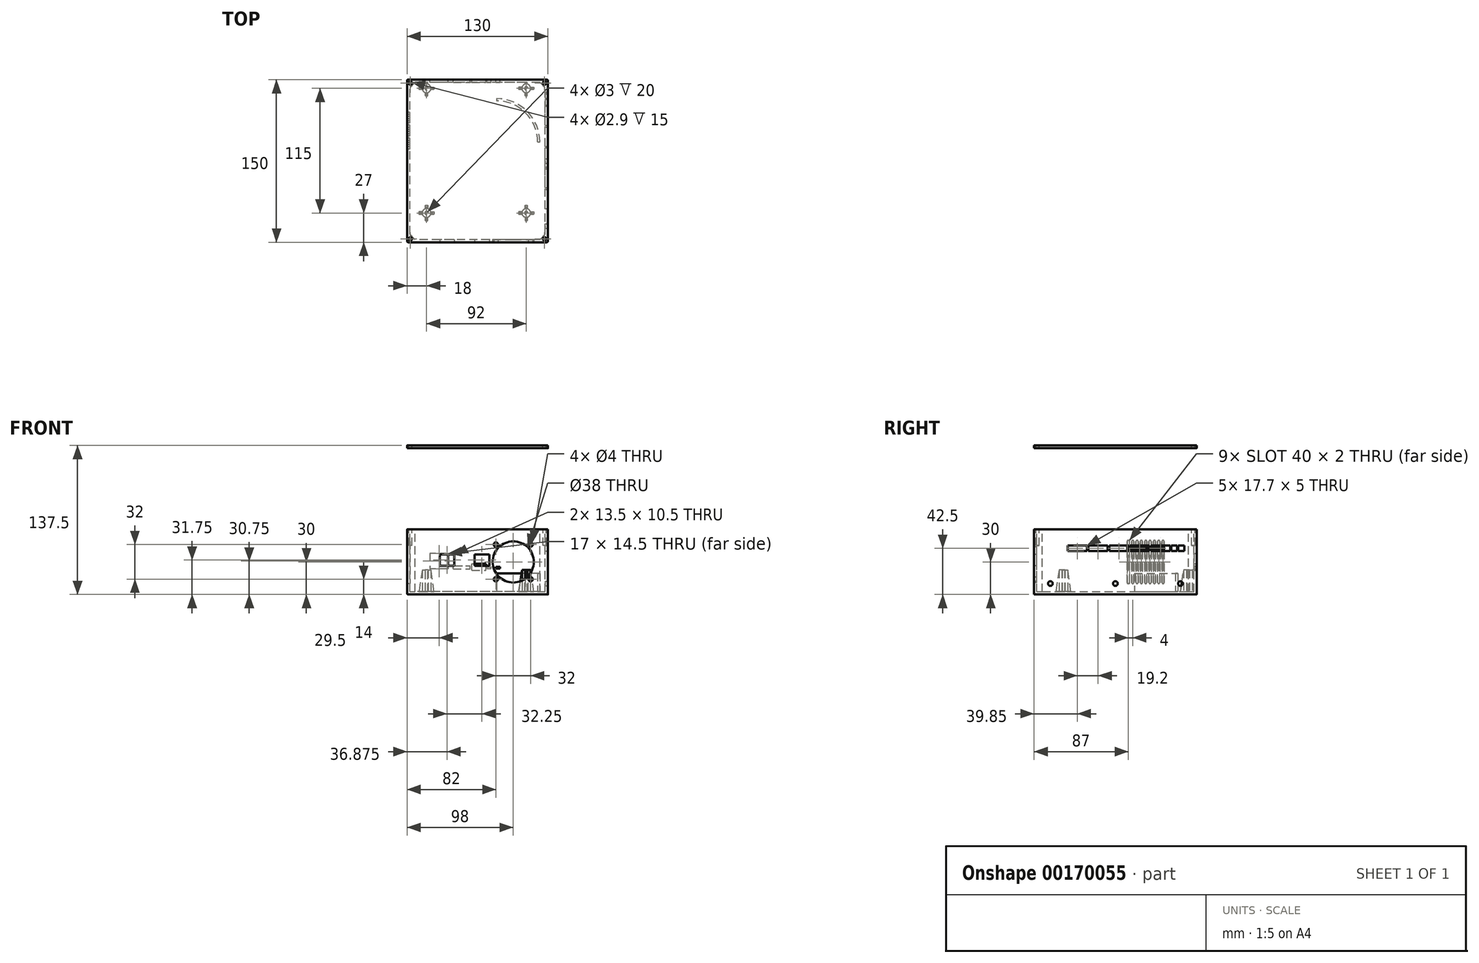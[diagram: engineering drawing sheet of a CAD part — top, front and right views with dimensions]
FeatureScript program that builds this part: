
annotation { "Feature Type Name" : "Feature", "Feature Type Description" : "" }
export const myFeature = defineFeature(function(context is Context, id is Id, definition is map)
    precondition{}
    {
        {
            var Q0;
            Q0=qCreatedBy(makeId("Top.planeOp"),FACE);
            var sketch = newSketch(context, id + "F0", { "sketchPlane" : qUnion([Q0])});
            skLineSegment(sketch, "E0.bottom", {"start": v(65, -75) * mm, "end": v(-65, -75) * mm});
            skLineSegment(sketch, "E0.top", {"start": v(65, 75) * mm, "end": v(-65, 75) * mm});
            skLineSegment(sketch, "E0.left", {"start": v(65, -75) * mm, "end": v(65, 75) * mm});
            skLineSegment(sketch, "E0.right", {"start": v(-65, -75) * mm, "end": v(-65, 75) * mm});
            skPoint(sketch, "E0.middle", {"position": v(0, 0) * mm});
            skCircle(sketch, "E1", {"center": v(-47, 67) * mm, "radius": 1.5 * mm});
            skCircle(sketch, "E2", {"center": v(45, 67) * mm, "radius": 1.5 * mm});
            skCircle(sketch, "E3", {"center": v(45, -48) * mm, "radius": 1.5 * mm});
            skCircle(sketch, "E4", {"center": v(-47, -48) * mm, "radius": 1.5 * mm});
            skCircle(sketch, "E5", {"center": v(-47, -48) * mm, "radius": 4 * mm});
            skCircle(sketch, "E6", {"center": v(45, -48) * mm, "radius": 4 * mm});
            skCircle(sketch, "E7", {"center": v(45, 67) * mm, "radius": 4 * mm});
            skCircle(sketch, "E8", {"center": v(-47, 67) * mm, "radius": 4 * mm});
            skLineSegment(sketch, "E9.bottom", {"start": v(46, 74) * mm, "end": v(44, 74) * mm});
            skLineSegment(sketch, "E9.top", {"start": v(46, 60) * mm, "end": v(44, 60) * mm});
            skLineSegment(sketch, "E9.left", {"start": v(46, 74) * mm, "end": v(46, 70.87) * mm});
            skLineSegment(sketch, "E9.right", {"start": v(44, 74) * mm, "end": v(44, 70.87) * mm});
            skLineSegment(sketch, "E10.bottom", {"start": v(52, 66) * mm, "end": v(48.87, 66) * mm});
            skLineSegment(sketch, "E10.top", {"start": v(52, 68) * mm, "end": v(48.87, 68) * mm});
            skLineSegment(sketch, "E10.left", {"start": v(52, 66) * mm, "end": v(52, 68) * mm});
            skLineSegment(sketch, "E10.right", {"start": v(38, 66) * mm, "end": v(38, 68) * mm});
            skLineSegment(sketch, "E11.trimOffspring", {"start": v(41.13, 68) * mm, "end": v(38, 68) * mm});
            skLineSegment(sketch, "E12.trimOffspring", {"start": v(41.13, 66) * mm, "end": v(38, 66) * mm});
            skLineSegment(sketch, "E13.trimOffspring", {"start": v(44, 63.13) * mm, "end": v(44, 60) * mm});
            skLineSegment(sketch, "E14.trimOffspring", {"start": v(46, 63.13) * mm, "end": v(46, 60) * mm});
            skLineSegment(sketch, "E15.bottom", {"start": v(-40, 66) * mm, "end": v(-43.13, 66) * mm});
            skLineSegment(sketch, "E15.top", {"start": v(-40, 68) * mm, "end": v(-43.13, 68) * mm});
            skLineSegment(sketch, "E15.left", {"start": v(-40, 66) * mm, "end": v(-40, 68) * mm});
            skLineSegment(sketch, "E15.right", {"start": v(-54, 66) * mm, "end": v(-54, 68) * mm});
            skLineSegment(sketch, "E16.bottom", {"start": v(-46, 74) * mm, "end": v(-48, 74) * mm});
            skLineSegment(sketch, "E16.top", {"start": v(-46, 60) * mm, "end": v(-48, 60) * mm});
            skLineSegment(sketch, "E16.left", {"start": v(-46, 74) * mm, "end": v(-46, 70.87) * mm});
            skLineSegment(sketch, "E16.right", {"start": v(-48, 74) * mm, "end": v(-48, 70.87) * mm});
            skLineSegment(sketch, "E17.trimOffspring", {"start": v(-50.87, 68) * mm, "end": v(-54, 68) * mm});
            skLineSegment(sketch, "E18.trimOffspring", {"start": v(-50.87, 66) * mm, "end": v(-54, 66) * mm});
            skLineSegment(sketch, "E19.trimOffspring", {"start": v(-48, 63.13) * mm, "end": v(-48, 60) * mm});
            skLineSegment(sketch, "E20.trimOffspring", {"start": v(-46, 63.13) * mm, "end": v(-46, 60) * mm});
            skLineSegment(sketch, "E21.bottom", {"start": v(-40, -49) * mm, "end": v(-43.13, -49) * mm});
            skLineSegment(sketch, "E21.top", {"start": v(-40, -47) * mm, "end": v(-43.13, -47) * mm});
            skLineSegment(sketch, "E21.left", {"start": v(-40, -49) * mm, "end": v(-40, -47) * mm});
            skLineSegment(sketch, "E21.right", {"start": v(-54, -49) * mm, "end": v(-54, -47) * mm});
            skLineSegment(sketch, "E22.bottom", {"start": v(-46, -41) * mm, "end": v(-48, -41) * mm});
            skLineSegment(sketch, "E22.top", {"start": v(-46, -55) * mm, "end": v(-48, -55) * mm});
            skLineSegment(sketch, "E22.left", {"start": v(-46, -41) * mm, "end": v(-46, -44.13) * mm});
            skLineSegment(sketch, "E22.right", {"start": v(-48, -41) * mm, "end": v(-48, -44.13) * mm});
            skLineSegment(sketch, "E23.trimOffspring", {"start": v(-50.87, -49) * mm, "end": v(-54, -49) * mm});
            skLineSegment(sketch, "E24.trimOffspring", {"start": v(-50.87, -47) * mm, "end": v(-54, -47) * mm});
            skLineSegment(sketch, "E25.trimOffspring", {"start": v(-46, -51.87) * mm, "end": v(-46, -55) * mm});
            skLineSegment(sketch, "E26.trimOffspring", {"start": v(-48, -51.87) * mm, "end": v(-48, -55) * mm});
            skLineSegment(sketch, "E27.bottom", {"start": v(52, -49) * mm, "end": v(48.87, -49) * mm});
            skLineSegment(sketch, "E27.top", {"start": v(52, -47) * mm, "end": v(48.87, -47) * mm});
            skLineSegment(sketch, "E27.left", {"start": v(52, -49) * mm, "end": v(52, -47) * mm});
            skLineSegment(sketch, "E27.right", {"start": v(38, -49) * mm, "end": v(38, -47) * mm});
            skLineSegment(sketch, "E28.bottom", {"start": v(46, -55) * mm, "end": v(44, -55) * mm});
            skLineSegment(sketch, "E28.top", {"start": v(46, -41) * mm, "end": v(44, -41) * mm});
            skLineSegment(sketch, "E28.left", {"start": v(46, -55) * mm, "end": v(46, -51.87) * mm});
            skLineSegment(sketch, "E28.right", {"start": v(44, -55) * mm, "end": v(44, -51.87) * mm});
            skLineSegment(sketch, "E29.trimOffspring", {"start": v(41.13, -49) * mm, "end": v(38, -49) * mm});
            skLineSegment(sketch, "E30.trimOffspring", {"start": v(41.13, -47) * mm, "end": v(38, -47) * mm});
            skLineSegment(sketch, "E31.trimOffspring", {"start": v(44, -44.13) * mm, "end": v(44, -41) * mm});
            skLineSegment(sketch, "E32.trimOffspring", {"start": v(46, -44.13) * mm, "end": v(46, -41) * mm});
            skLineSegment(sketch, "E33", {"start": v(65, 65) * mm, "end": v(55, 75) * mm});
            skLineSegment(sketch, "E34", {"start": v(65, -65) * mm, "end": v(55, -75) * mm});
            skLineSegment(sketch, "E35", {"start": v(-55, 75) * mm, "end": v(-65, 65) * mm});
            skLineSegment(sketch, "E36", {"start": v(-65, -65) * mm, "end": v(-55, -75) * mm});
            skSolve(sketch);
        }
        {
            var Q0;
            Q0=makeQuery(id+"F0.imprint","IMPRINT",FACE,{"disambiguationData":[TD([[makeQuery(id+"F0.imprint","IMPRINT",EDGE,{"derivedFrom":sQuery(id+"F0.wireOp",EDGE,"E0.bottom")}),-1.0]])]});
            var Q1;
            Q1=makeQuery(id+"F0.imprint","IMPRINT",FACE,{"disambiguationData":[TD([[makeQuery(id+"F0.imprint","IMPRINT",EDGE,{"derivedFrom":sQuery(id+"F0.wireOp",EDGE,"E2")}),-1.0]])]});
            var Q2;
            Q2=makeQuery(id+"F0.imprint","IMPRINT",FACE,{"disambiguationData":[TD([[makeQuery(id+"F0.imprint","IMPRINT",EDGE,{"derivedFrom":sQuery(id+"F0.wireOp",EDGE,"E4")}),-1.0]])]});
            var Q3;
            Q3=makeQuery(id+"F0.imprint","IMPRINT",FACE,{"disambiguationData":[TD([[makeQuery(id+"F0.imprint","IMPRINT",EDGE,{"derivedFrom":sQuery(id+"F0.wireOp",EDGE,"E16.top")}),-1.0]])]});
            var Q4;
            Q4=makeQuery(id+"F0.imprint","IMPRINT",FACE,{"disambiguationData":[TD([[makeQuery(id+"F0.imprint","IMPRINT",EDGE,{"derivedFrom":sQuery(id+"F0.wireOp",EDGE,"E21.right")}),-1.0]])]});
            var Q5;
            Q5=makeQuery(id+"F0.imprint","IMPRINT",FACE,{"disambiguationData":[TD([[makeQuery(id+"F0.imprint","IMPRINT",EDGE,{"derivedFrom":sQuery(id+"F0.wireOp",EDGE,"E22.top")}),-1.0]])]});
            var Q6;
            Q6=makeQuery(id+"F0.imprint","IMPRINT",FACE,{"disambiguationData":[TD([[makeQuery(id+"F0.imprint","IMPRINT",EDGE,{"derivedFrom":sQuery(id+"F0.wireOp",EDGE,"E1")}),-1.0]])]});
            var Q7;
            Q7=makeQuery(id+"F0.imprint","IMPRINT",FACE,{"disambiguationData":[TD([[makeQuery(id+"F0.imprint","IMPRINT",EDGE,{"derivedFrom":sQuery(id+"F0.wireOp",EDGE,"E3")}),-1.0]])]});
            var Q8;
            Q8=makeQuery(id+"F0.imprint","IMPRINT",FACE,{"disambiguationData":[TD([[makeQuery(id+"F0.imprint","IMPRINT",EDGE,{"derivedFrom":sQuery(id+"F0.wireOp",EDGE,"E15.right")}),-1.0]])]});
            var Q9;
            Q9=makeQuery(id+"F0.imprint","IMPRINT",FACE,{"disambiguationData":[TD([[makeQuery(id+"F0.imprint","IMPRINT",EDGE,{"derivedFrom":sQuery(id+"F0.wireOp",EDGE,"E28.bottom")}),-1.0]])]});
            var Q10;
            {var subQ0=sQuery(id+"F0.wireOp",EDGE,"E10.bottom");Q10=makeQuery(id+"F0.imprint","IMPRINT",FACE,{"disambiguationData":[TD([[makeQuery(id+"F0.imprint","IMPRINT",EDGE,{"derivedFrom":subQ0}),-1.0]])]});}
            var Q11;
            Q11=makeQuery(id+"F0.imprint","IMPRINT",FACE,{"disambiguationData":[TD([[makeQuery(id+"F0.imprint","IMPRINT",EDGE,{"derivedFrom":sQuery(id+"F0.wireOp",EDGE,"E9.top")}),-1.0]])]});
            var Q12;
            {var subQ0=sQuery(id+"F0.wireOp",EDGE,"E21.bottom");Q12=makeQuery(id+"F0.imprint","IMPRINT",FACE,{"disambiguationData":[TD([[makeQuery(id+"F0.imprint","IMPRINT",EDGE,{"derivedFrom":subQ0}),-1.0]])]});}
            var Q13;
            Q13=makeQuery(id+"F0.imprint","IMPRINT",FACE,{"disambiguationData":[TD([[makeQuery(id+"F0.imprint","IMPRINT",EDGE,{"derivedFrom":sQuery(id+"F0.wireOp",EDGE,"E28.top")}),1.0]])]});
            var Q14;
            Q14=makeQuery(id+"F0.imprint","IMPRINT",FACE,{"disambiguationData":[TD([[makeQuery(id+"F0.imprint","IMPRINT",EDGE,{"derivedFrom":sQuery(id+"F0.wireOp",EDGE,"E27.right")}),-1.0]])]});
            var Q15;
            Q15=makeQuery(id+"F0.imprint","IMPRINT",FACE,{"disambiguationData":[TD([[makeQuery(id+"F0.imprint","IMPRINT",EDGE,{"derivedFrom":sQuery(id+"F0.wireOp",EDGE,"E22.bottom")}),1.0]])]});
            var Q16;
            {var subQ0=sQuery(id+"F0.wireOp",EDGE,"E15.bottom");Q16=makeQuery(id+"F0.imprint","IMPRINT",FACE,{"disambiguationData":[TD([[makeQuery(id+"F0.imprint","IMPRINT",EDGE,{"derivedFrom":subQ0}),-1.0]])]});}
            var Q17;
            Q17=makeQuery(id+"F0.imprint","IMPRINT",FACE,{"disambiguationData":[TD([[makeQuery(id+"F0.imprint","IMPRINT",EDGE,{"derivedFrom":sQuery(id+"F0.wireOp",EDGE,"E9.bottom")}),1.0]])]});
            var Q18;
            {var subQ0=sQuery(id+"F0.wireOp",EDGE,"E27.bottom");Q18=makeQuery(id+"F0.imprint","IMPRINT",FACE,{"disambiguationData":[TD([[makeQuery(id+"F0.imprint","IMPRINT",EDGE,{"derivedFrom":subQ0}),-1.0]])]});}
            var Q19;
            Q19=makeQuery(id+"F0.imprint","IMPRINT",FACE,{"disambiguationData":[TD([[makeQuery(id+"F0.imprint","IMPRINT",EDGE,{"derivedFrom":sQuery(id+"F0.wireOp",EDGE,"E10.right")}),-1.0]])]});
            var Q20;
            Q20=makeQuery(id+"F0.imprint","IMPRINT",FACE,{"disambiguationData":[TD([[makeQuery(id+"F0.imprint","IMPRINT",EDGE,{"derivedFrom":sQuery(id+"F0.wireOp",EDGE,"E16.bottom")}),1.0]])]});
            var Q21;
            Q21=makeQuery(id+"F0.imprint","IMPRINT",FACE,{"disambiguationData":[TD([[makeQuery(id+"F0.imprint","IMPRINT",EDGE,{"derivedFrom":sQuery(id+"F0.wireOp",EDGE,"E2")}),1.0]])]});
            var Q22;
            Q22=makeQuery(id+"F0.imprint","IMPRINT",FACE,{"disambiguationData":[TD([[makeQuery(id+"F0.imprint","IMPRINT",EDGE,{"derivedFrom":sQuery(id+"F0.wireOp",EDGE,"E1")}),1.0]])]});
            var Q23;
            Q23=makeQuery(id+"F0.imprint","IMPRINT",FACE,{"disambiguationData":[TD([[makeQuery(id+"F0.imprint","IMPRINT",EDGE,{"derivedFrom":sQuery(id+"F0.wireOp",EDGE,"E4")}),1.0]])]});
            var Q24;
            Q24=makeQuery(id+"F0.imprint","IMPRINT",FACE,{"disambiguationData":[TD([[makeQuery(id+"F0.imprint","IMPRINT",EDGE,{"derivedFrom":sQuery(id+"F0.wireOp",EDGE,"E3")}),1.0]])]});
            var Q25;
            Q25=makeQuery(id+"F0.imprint","IMPRINT",FACE,{"disambiguationData":[TD([[makeQuery(id+"F0.imprint","IMPRINT",EDGE,{"derivedFrom":sQuery(id+"F0.wireOp",EDGE,"E9.bottom")}),-1.0]])]});
            var Q26;
            {var subQ3=sQuery(id+"F0.wireOp",EDGE,"E33");Q26=makeQuery(id+"F0.imprint","IMPRINT",FACE,{"disambiguationData":[TD([[makeQuery(id+"F0.imprint","IMPRINT",EDGE,{"derivedFrom":subQ3}),-1.0]])]});}
            var Q27;
            {var subQ3=sQuery(id+"F0.wireOp",EDGE,"E35");Q27=makeQuery(id+"F0.imprint","IMPRINT",FACE,{"disambiguationData":[TD([[makeQuery(id+"F0.imprint","IMPRINT",EDGE,{"derivedFrom":subQ3}),-1.0]])]});}
            extrude(context, id + "F1", {"entities" : qUnion([Q0, Q1, Q2, Q3, Q4, Q5, Q6, Q7, Q8, Q9, Q10, Q11, Q12, Q13, Q14, Q15, Q16, Q17, Q18, Q19, Q20, Q21, Q22, Q23, Q24, Q25, Q26, Q27]), "depth" : 60 * mm});
        }
        {
            var Q0;
            Q0=makeQuery(id+"F1.opExtrude","CAP_FACE",FACE,{"disambiguationData":[OSD([sQuery(id+"F0.wireOp",EDGE,"E0.bottom"),sQuery(id+"F0.wireOp",EDGE,"E0.top"),sQuery(id+"F0.wireOp",EDGE,"E0.left"),sQuery(id+"F0.wireOp",EDGE,"E0.right")])],"isStart":false});
            shell(context, id + "F2", {"entities" : qUnion([Q0]), "thickness" : 2.5 * mm});
        }
        {
            var Q0;
            Q0=makeQuery(id+"F0.imprint","IMPRINT",FACE,{"disambiguationData":[TD([[makeQuery(id+"F0.imprint","IMPRINT",EDGE,{"derivedFrom":sQuery(id+"F0.wireOp",EDGE,"E1")}),-1.0]])]});
            var Q1;
            Q1=makeQuery(id+"F0.imprint","IMPRINT",FACE,{"disambiguationData":[TD([[makeQuery(id+"F0.imprint","IMPRINT",EDGE,{"derivedFrom":sQuery(id+"F0.wireOp",EDGE,"E4")}),-1.0]])]});
            var Q2;
            Q2=makeQuery(id+"F0.imprint","IMPRINT",FACE,{"disambiguationData":[TD([[makeQuery(id+"F0.imprint","IMPRINT",EDGE,{"derivedFrom":sQuery(id+"F0.wireOp",EDGE,"E3")}),-1.0]])]});
            var Q3;
            Q3=makeQuery(id+"F0.imprint","IMPRINT",FACE,{"disambiguationData":[TD([[makeQuery(id+"F0.imprint","IMPRINT",EDGE,{"derivedFrom":sQuery(id+"F0.wireOp",EDGE,"E2")}),-1.0]])]});
            var Q4;
            {var subQ0=sQuery(id+"F0.wireOp",EDGE,"E10.bottom");Q4=makeQuery(id+"F0.imprint","IMPRINT",FACE,{"disambiguationData":[TD([[makeQuery(id+"F0.imprint","IMPRINT",EDGE,{"derivedFrom":subQ0}),-1.0]])]});}
            var Q5;
            Q5=makeQuery(id+"F0.imprint","IMPRINT",FACE,{"disambiguationData":[TD([[makeQuery(id+"F0.imprint","IMPRINT",EDGE,{"derivedFrom":sQuery(id+"F0.wireOp",EDGE,"E9.top")}),-1.0]])]});
            var Q6;
            Q6=makeQuery(id+"F0.imprint","IMPRINT",FACE,{"disambiguationData":[TD([[makeQuery(id+"F0.imprint","IMPRINT",EDGE,{"derivedFrom":sQuery(id+"F0.wireOp",EDGE,"E10.right")}),-1.0]])]});
            var Q7;
            Q7=makeQuery(id+"F0.imprint","IMPRINT",FACE,{"disambiguationData":[TD([[makeQuery(id+"F0.imprint","IMPRINT",EDGE,{"derivedFrom":sQuery(id+"F0.wireOp",EDGE,"E9.bottom")}),1.0]])]});
            var Q8;
            Q8=makeQuery(id+"F0.imprint","IMPRINT",FACE,{"disambiguationData":[TD([[makeQuery(id+"F0.imprint","IMPRINT",EDGE,{"derivedFrom":sQuery(id+"F0.wireOp",EDGE,"E16.bottom")}),1.0]])]});
            var Q9;
            Q9=makeQuery(id+"F0.imprint","IMPRINT",FACE,{"disambiguationData":[TD([[makeQuery(id+"F0.imprint","IMPRINT",EDGE,{"derivedFrom":sQuery(id+"F0.wireOp",EDGE,"E15.right")}),-1.0]])]});
            var Q10;
            Q10=makeQuery(id+"F0.imprint","IMPRINT",FACE,{"disambiguationData":[TD([[makeQuery(id+"F0.imprint","IMPRINT",EDGE,{"derivedFrom":sQuery(id+"F0.wireOp",EDGE,"E16.top")}),-1.0]])]});
            var Q11;
            {var subQ0=sQuery(id+"F0.wireOp",EDGE,"E15.bottom");Q11=makeQuery(id+"F0.imprint","IMPRINT",FACE,{"disambiguationData":[TD([[makeQuery(id+"F0.imprint","IMPRINT",EDGE,{"derivedFrom":subQ0}),-1.0]])]});}
            var Q12;
            {var subQ0=sQuery(id+"F0.wireOp",EDGE,"E21.bottom");Q12=makeQuery(id+"F0.imprint","IMPRINT",FACE,{"disambiguationData":[TD([[makeQuery(id+"F0.imprint","IMPRINT",EDGE,{"derivedFrom":subQ0}),-1.0]])]});}
            var Q13;
            Q13=makeQuery(id+"F0.imprint","IMPRINT",FACE,{"disambiguationData":[TD([[makeQuery(id+"F0.imprint","IMPRINT",EDGE,{"derivedFrom":sQuery(id+"F0.wireOp",EDGE,"E22.bottom")}),1.0]])]});
            var Q14;
            Q14=makeQuery(id+"F0.imprint","IMPRINT",FACE,{"disambiguationData":[TD([[makeQuery(id+"F0.imprint","IMPRINT",EDGE,{"derivedFrom":sQuery(id+"F0.wireOp",EDGE,"E21.right")}),-1.0]])]});
            var Q15;
            Q15=makeQuery(id+"F0.imprint","IMPRINT",FACE,{"disambiguationData":[TD([[makeQuery(id+"F0.imprint","IMPRINT",EDGE,{"derivedFrom":sQuery(id+"F0.wireOp",EDGE,"E22.top")}),-1.0]])]});
            var Q16;
            Q16=makeQuery(id+"F0.imprint","IMPRINT",FACE,{"disambiguationData":[TD([[makeQuery(id+"F0.imprint","IMPRINT",EDGE,{"derivedFrom":sQuery(id+"F0.wireOp",EDGE,"E27.right")}),-1.0]])]});
            var Q17;
            Q17=makeQuery(id+"F0.imprint","IMPRINT",FACE,{"disambiguationData":[TD([[makeQuery(id+"F0.imprint","IMPRINT",EDGE,{"derivedFrom":sQuery(id+"F0.wireOp",EDGE,"E28.top")}),1.0]])]});
            var Q18;
            {var subQ0=sQuery(id+"F0.wireOp",EDGE,"E27.bottom");Q18=makeQuery(id+"F0.imprint","IMPRINT",FACE,{"disambiguationData":[TD([[makeQuery(id+"F0.imprint","IMPRINT",EDGE,{"derivedFrom":subQ0}),-1.0]])]});}
            var Q19;
            Q19=makeQuery(id+"F0.imprint","IMPRINT",FACE,{"disambiguationData":[TD([[makeQuery(id+"F0.imprint","IMPRINT",EDGE,{"derivedFrom":sQuery(id+"F0.wireOp",EDGE,"E28.bottom")}),-1.0]])]});
            extrude(context, id + "F3", {"entities" : qUnion([Q0, Q1, Q2, Q3, Q4, Q5, Q6, Q7, Q8, Q9, Q10, Q11, Q12, Q13, Q14, Q15, Q16, Q17, Q18, Q19]), "operationType" : NewBodyOperationType.ADD, "depth" : (20 + 2.5) * mm});
        }
        {
            var Q0;
            Q0=makeQuery(id+"F1.opExtrude","SWEPT_FACE",FACE,{"disambiguationData":[OSD([sQuery(id+"F0.wireOp",EDGE,"E0.top")])]});
            var sketch = newSketch(context, id + "F4", { "sketchPlane" : qUnion([Q0])});
            skLineSegment(sketch, "E37.bottom", {"start": v(27, 38) * mm, "end": v(44, 38) * mm});
            skLineSegment(sketch, "E37.top", {"start": v(27, 23.5) * mm, "end": v(44, 23.5) * mm});
            skLineSegment(sketch, "E37.left", {"start": v(27, 38) * mm, "end": v(27, 23.5) * mm});
            skLineSegment(sketch, "E37.right", {"start": v(44, 38) * mm, "end": v(44, 23.5) * mm});
            skLineSegment(sketch, "E38.bottom", {"start": v(22.5, 23.5) * mm, "end": v(6.7, 23.5) * mm});
            skLineSegment(sketch, "E38.top", {"start": v(22.5, 26.5) * mm, "end": v(6.7, 26.5) * mm});
            skLineSegment(sketch, "E38.left", {"start": v(22.5, 23.5) * mm, "end": v(22.5, 26.5) * mm});
            skLineSegment(sketch, "E38.right", {"start": v(6.7, 23.5) * mm, "end": v(6.7, 26.5) * mm});
            skLineSegment(sketch, "E39.bottom", {"start": v(5.25, 22.4) * mm, "end": v(-7.75, 22.4) * mm});
            skLineSegment(sketch, "E39.top", {"start": v(5.25, 28.4) * mm, "end": v(-7.75, 28.4) * mm});
            skLineSegment(sketch, "E39.left", {"start": v(5.25, 22.4) * mm, "end": v(5.25, 28.4) * mm});
            skLineSegment(sketch, "E39.right", {"start": v(-7.75, 22.4) * mm, "end": v(-7.75, 28.4) * mm});
            skLineSegment(sketch, "E40.bottom", {"start": v(-8.65, 24) * mm, "end": v(-12.65, 24) * mm});
            skLineSegment(sketch, "E40.top", {"start": v(-8.65, 25.45) * mm, "end": v(-12.65, 25.45) * mm});
            skLineSegment(sketch, "E40.left", {"start": v(-8.65, 24) * mm, "end": v(-8.65, 25.45) * mm});
            skLineSegment(sketch, "E40.right", {"start": v(-12.65, 24) * mm, "end": v(-12.65, 25.45) * mm});
            skLineSegment(sketch, "E41.bottom", {"start": v(-16.95, 24) * mm, "end": v(-20.95, 24) * mm});
            skLineSegment(sketch, "E41.top", {"start": v(-16.95, 25.45) * mm, "end": v(-20.95, 25.45) * mm});
            skLineSegment(sketch, "E41.left", {"start": v(-16.95, 24) * mm, "end": v(-16.95, 25.45) * mm});
            skLineSegment(sketch, "E41.right", {"start": v(-20.95, 24) * mm, "end": v(-20.95, 25.45) * mm});
            skSolve(sketch);
        }
        {
            var Q0;
            Q0=qSketchRegion(id+"F4",true);
            extrude(context, id + "F5", {"entities" : qUnion([Q0]), "operationType" : NewBodyOperationType.REMOVE, "endBound" : BoundingType.UP_TO_NEXT, "oppositeDirection" : true, "depth" : 25 * mm});
        }
        {
            var Q0;
            Q0=makeQuery(id+"F1.opExtrude","SWEPT_FACE",FACE,{"disambiguationData":[OSD([sQuery(id+"F0.wireOp",EDGE,"E0.bottom")])]});
            var sketch = newSketch(context, id + "F6", { "sketchPlane" : qUnion([Q0])});
            skCircle(sketch, "E42", {"center": v(33, 30) * mm, "radius": 19 * mm});
            skPoint(sketch, "E42.centerSnap0", {"position": v(13, 30) * mm});
            skPoint(sketch, "E42.centerSnap1", {"position": v(33, 50) * mm});
            skCircle(sketch, "E43", {"center": v(17, 46) * mm, "radius": 2 * mm});
            skCircle(sketch, "E44", {"center": v(49, 46) * mm, "radius": 2 * mm});
            skCircle(sketch, "E45", {"center": v(49, 14) * mm, "radius": 2 * mm});
            skCircle(sketch, "E46", {"center": v(17, 14) * mm, "radius": 2 * mm});
            skLineSegment(sketch, "E47.bottom", {"start": v(17, 14) * mm, "end": v(49, 14) * mm, "construction": true});
            skLineSegment(sketch, "E47.top", {"start": v(17, 46) * mm, "end": v(49, 46) * mm, "construction": true});
            skLineSegment(sketch, "E47.left", {"start": v(17, 14) * mm, "end": v(17, 46) * mm, "construction": true});
            skLineSegment(sketch, "E47.right", {"start": v(49, 14) * mm, "end": v(49, 46) * mm, "construction": true});
            skLineSegment(sketch, "E48.bottom", {"start": v(-2.63, 37) * mm, "end": v(10.87, 37) * mm});
            skLineSegment(sketch, "E48.top", {"start": v(-2.63, 26.5) * mm, "end": v(10.87, 26.5) * mm});
            skLineSegment(sketch, "E48.left", {"start": v(-2.63, 37) * mm, "end": v(-2.63, 26.5) * mm});
            skLineSegment(sketch, "E48.right", {"start": v(10.87, 37) * mm, "end": v(10.87, 26.5) * mm});
            skLineSegment(sketch, "E49.bottom", {"start": v(-34.88, 37) * mm, "end": v(-21.38, 37) * mm});
            skLineSegment(sketch, "E49.top", {"start": v(-34.88, 26.5) * mm, "end": v(-21.38, 26.5) * mm});
            skLineSegment(sketch, "E49.left", {"start": v(-34.88, 37) * mm, "end": v(-34.88, 26.5) * mm});
            skLineSegment(sketch, "E49.right", {"start": v(-21.38, 37) * mm, "end": v(-21.38, 26.5) * mm});
            skSolve(sketch);
        }
        {
            var Q0;
            Q0=qSketchRegion(id+"F6",true);
            extrude(context, id + "F7", {"entities" : qUnion([Q0]), "operationType" : NewBodyOperationType.REMOVE, "endBound" : BoundingType.UP_TO_NEXT, "oppositeDirection" : true, "depth" : 25 * mm});
        }
        {
            var Q0;
            Q0=makeQuery(id+"F1.opExtrude","SWEPT_FACE",FACE,{"disambiguationData":[OSD([sQuery(id+"F0.wireOp",EDGE,"E0.left")])]});
            var sketch = newSketch(context, id + "F8", { "sketchPlane" : qUnion([Q0])});
            skLineSegment(sketch, "E50.bottom", {"start": v(-75, 0) * mm, "end": v(75, 0) * mm, "construction": true});
            skLineSegment(sketch, "E50.top", {"start": v(-75, 20) * mm, "end": v(75, 20) * mm, "construction": true});
            skLineSegment(sketch, "E50.left", {"start": v(-75, 0) * mm, "end": v(-75, 20) * mm, "construction": true});
            skLineSegment(sketch, "E50.right", {"start": v(75, 0) * mm, "end": v(75, 20) * mm, "construction": true});
            skCircle(sketch, "E51", {"center": v(-60, 10) * mm, "radius": 2.15 * mm});
            skPoint(sketch, "E51.centerSnap0", {"position": v(-75, 10) * mm});
            skCircle(sketch, "E52", {"center": v(60, 10) * mm, "radius": 2.15 * mm});
            skCircle(sketch, "E53", {"center": v(0, 10) * mm, "radius": 2.15 * mm});
            skPoint(sketch, "E53.centerSnap0", {"position": v(0, 0) * mm});
            skPoint(sketch, "E54.firstSnap0", {"position": v(-75, 40) * mm});
            skLineSegment(sketch, "E54.bottom", {"start": v(-44, 40) * mm, "end": v(-26.3, 40) * mm});
            skLineSegment(sketch, "E54.top", {"start": v(-44, 45) * mm, "end": v(-26.3, 45) * mm});
            skLineSegment(sketch, "E54.left", {"start": v(-44, 40) * mm, "end": v(-44, 45) * mm});
            skLineSegment(sketch, "E54.right", {"start": v(63.5, 40) * mm, "end": v(63.5, 45) * mm});
            skLineSegment(sketch, "E55.bottom", {"start": v(63.5, 45) * mm, "end": v(58, 45) * mm});
            skLineSegment(sketch, "E55.top", {"start": v(63.5, 40) * mm, "end": v(58, 40) * mm});
            skLineSegment(sketch, "E55.left", {"start": v(63.5, 45) * mm, "end": v(63.5, 40) * mm});
            skLineSegment(sketch, "E55.right", {"start": v(58, 45) * mm, "end": v(58, 40) * mm});
            skLineSegment(sketch, "E56.bottom", {"start": v(57, 45) * mm, "end": v(51.5, 45) * mm});
            skLineSegment(sketch, "E56.top", {"start": v(57, 40) * mm, "end": v(51.5, 40) * mm});
            skLineSegment(sketch, "E56.left", {"start": v(57, 45) * mm, "end": v(57, 40) * mm});
            skLineSegment(sketch, "E56.right", {"start": v(51.5, 45) * mm, "end": v(51.5, 40) * mm});
            skLineSegment(sketch, "E57.trimOffspring", {"start": v(58, 45) * mm, "end": v(63.5, 45) * mm});
            skLineSegment(sketch, "E58.trimOffspring", {"start": v(58, 40) * mm, "end": v(63.5, 40) * mm});
            skLineSegment(sketch, "E59", {"start": v(50.5, 45) * mm, "end": v(50.5, 40) * mm});
            skLineSegment(sketch, "E60.trimOffspring", {"start": v(51.5, 45) * mm, "end": v(57, 45) * mm});
            skLineSegment(sketch, "E61.trimOffspring", {"start": v(51.5, 40) * mm, "end": v(57, 40) * mm});
            skLineSegment(sketch, "E62.left", {"start": v(31.3, 45) * mm, "end": v(31.3, 40) * mm});
            skLineSegment(sketch, "E62.right", {"start": v(32.8, 45) * mm, "end": v(32.8, 40) * mm});
            skLineSegment(sketch, "E63.trimOffspring", {"start": v(32.8, 45) * mm, "end": v(50.5, 45) * mm});
            skLineSegment(sketch, "E64.trimOffspring", {"start": v(32.8, 40) * mm, "end": v(50.5, 40) * mm});
            skLineSegment(sketch, "E65.left", {"start": v(12.1, 45) * mm, "end": v(12.1, 40) * mm});
            skLineSegment(sketch, "E65.right", {"start": v(13.6, 45) * mm, "end": v(13.6, 40) * mm});
            skLineSegment(sketch, "E66.left", {"start": v(-7.1, 45) * mm, "end": v(-7.1, 40) * mm});
            skLineSegment(sketch, "E66.right", {"start": v(-5.6, 45) * mm, "end": v(-5.6, 40) * mm});
            skLineSegment(sketch, "E67.trimOffspring", {"start": v(-5.6, 45) * mm, "end": v(12.1, 45) * mm});
            skLineSegment(sketch, "E68.trimOffspring", {"start": v(-5.6, 40) * mm, "end": v(12.1, 40) * mm});
            skLineSegment(sketch, "E69.trimOffspring", {"start": v(13.6, 45) * mm, "end": v(31.3, 45) * mm});
            skLineSegment(sketch, "E70.trimOffspring", {"start": v(13.6, 40) * mm, "end": v(31.3, 40) * mm});
            skLineSegment(sketch, "E71.left", {"start": v(-26.3, 45) * mm, "end": v(-26.3, 40) * mm});
            skLineSegment(sketch, "E71.right", {"start": v(-24.8, 45) * mm, "end": v(-24.8, 40) * mm});
            skLineSegment(sketch, "E72.trimOffspring", {"start": v(-24.8, 45) * mm, "end": v(-7.1, 45) * mm});
            skLineSegment(sketch, "E73.trimOffspring", {"start": v(-24.8, 40) * mm, "end": v(-7.1, 40) * mm});
            skLineSegment(sketch, "E74", {"start": v(-44, 45) * mm, "end": v(12.1, 45) * mm, "construction": true});
            skLineSegment(sketch, "E75", {"start": v(12.1, 40) * mm, "end": v(-44, 40) * mm, "construction": true});
            skLineSegment(sketch, "E76", {"start": v(13.6, 40) * mm, "end": v(63.5, 40) * mm, "construction": true});
            skLineSegment(sketch, "E77", {"start": v(63.5, 45) * mm, "end": v(13.6, 45) * mm, "construction": true});
            skSolve(sketch);
        }
        {
            var Q0;
            Q0=qSketchRegion(id+"F8",true);
            extrude(context, id + "F9", {"entities" : qUnion([Q0]), "operationType" : NewBodyOperationType.REMOVE, "endBound" : BoundingType.UP_TO_NEXT, "oppositeDirection" : true, "depth" : 25 * mm});
        }
        {
            var Q0;
            {var subQ0=sQuery(id+"F0.wireOp",EDGE,"E0.right");var subQ1=sQuery(id+"F0.wireOp",EDGE,"E0.left");var subQ2=sQuery(id+"F0.wireOp",EDGE,"E0.top");var subQ3=sQuery(id+"F0.wireOp",EDGE,"E0.bottom");Q0=makeQuery(id+"F3.boolean.opBoolean","SPLIT",FACE,{"disambiguationData":[TD([makeQuery(id+"F2.opShell","OFFSET_FACE",FACE,{"disambiguationData":[OSD([subQ3])]})])],"derivedFrom":makeQuery(id+"F2.opShell","OFFSET_FACE",FACE,{"disambiguationData":[OSD([subQ3,subQ2,subQ1,subQ0])]})});}
            var sketch = newSketch(context, id + "F10", { "sketchPlane" : qUnion([Q0])});
            skArc(sketch, "E78", {"start": v(57.5, 17.5) * mm, "mid": v(45.78, 45.78) * mm, "end": v(17.5, 57.5) * mm});
            skArc(sketch, "E79.0", {"start": v(55.5, 17.5) * mm, "mid": v(44.37, 44.37) * mm, "end": v(17.5, 55.5) * mm});
            skLineSegment(sketch, "E80", {"start": v(17.5, 57.5) * mm, "end": v(17.5, 55.5) * mm});
            skLineSegment(sketch, "E81", {"start": v(55.5, 17.5) * mm, "end": v(57.5, 17.5) * mm});
            skSolve(sketch);
        }
        {
            var Q0;
            Q0=makeQuery(id+"F10.imprint","IMPRINT",FACE,{"disambiguationData":[TD([[makeQuery(id+"F10.imprint","IMPRINT",EDGE,{"derivedFrom":sQuery(id+"F10.wireOp",EDGE,"E78")}),1.0]])]});
            extrude(context, id + "F11", {"entities" : qUnion([Q0]), "operationType" : NewBodyOperationType.ADD, "depth" : 17 * mm});
        }
        {
            var Q0;
            Q0=makeQuery(id+"F1.opExtrude","SWEPT_FACE",FACE,{"disambiguationData":[OSD([sQuery(id+"F0.wireOp",EDGE,"E0.right")])]});
            var sketch = newSketch(context, id + "F12", { "sketchPlane" : qUnion([Q0])});
            skLineSegment(sketch, "E82.bottom", {"start": v(-45, 10) * mm, "end": v(-43, 10) * mm});
            skLineSegment(sketch, "E82.top", {"start": v(-45, 50) * mm, "end": v(-43, 50) * mm});
            skLineSegment(sketch, "E82.left", {"start": v(-45, 10) * mm, "end": v(-45, 50) * mm});
            skLineSegment(sketch, "E82.right", {"start": v(-43, 10) * mm, "end": v(-43, 50) * mm});
            skLineSegment(sketch, "E83.1.0.0", {"start": v(-39, 10) * mm, "end": v(-39, 50) * mm});
            skLineSegment(sketch, "E83.1.0.1", {"start": v(-41, 10) * mm, "end": v(-41, 50) * mm});
            skLineSegment(sketch, "E83.1.0.2", {"start": v(-41, 50) * mm, "end": v(-39, 50) * mm});
            skLineSegment(sketch, "E83.1.0.3", {"start": v(-41, 10) * mm, "end": v(-39, 10) * mm});
            skLineSegment(sketch, "E83.2.0.0", {"start": v(-35, 10) * mm, "end": v(-35, 50) * mm});
            skLineSegment(sketch, "E83.2.0.1", {"start": v(-37, 10) * mm, "end": v(-37, 50) * mm});
            skLineSegment(sketch, "E83.2.0.2", {"start": v(-37, 50) * mm, "end": v(-35, 50) * mm});
            skLineSegment(sketch, "E83.2.0.3", {"start": v(-37, 10) * mm, "end": v(-35, 10) * mm});
            skLineSegment(sketch, "E83.3.0.0", {"start": v(-31, 10) * mm, "end": v(-31, 50) * mm});
            skLineSegment(sketch, "E83.3.0.1", {"start": v(-33, 10) * mm, "end": v(-33, 50) * mm});
            skLineSegment(sketch, "E83.3.0.2", {"start": v(-33, 50) * mm, "end": v(-31, 50) * mm});
            skLineSegment(sketch, "E83.3.0.3", {"start": v(-33, 10) * mm, "end": v(-31, 10) * mm});
            skLineSegment(sketch, "E83.4.0.0", {"start": v(-27, 10) * mm, "end": v(-27, 50) * mm});
            skLineSegment(sketch, "E83.4.0.1", {"start": v(-29, 10) * mm, "end": v(-29, 50) * mm});
            skLineSegment(sketch, "E83.4.0.2", {"start": v(-29, 50) * mm, "end": v(-27, 50) * mm});
            skLineSegment(sketch, "E83.4.0.3", {"start": v(-29, 10) * mm, "end": v(-27, 10) * mm});
            skLineSegment(sketch, "E83.5.0.0", {"start": v(-23, 10) * mm, "end": v(-23, 50) * mm});
            skLineSegment(sketch, "E83.5.0.1", {"start": v(-25, 10) * mm, "end": v(-25, 50) * mm});
            skLineSegment(sketch, "E83.5.0.2", {"start": v(-25, 50) * mm, "end": v(-23, 50) * mm});
            skLineSegment(sketch, "E83.5.0.3", {"start": v(-25, 10) * mm, "end": v(-23, 10) * mm});
            skLineSegment(sketch, "E83.6.0.0", {"start": v(-19, 10) * mm, "end": v(-19, 50) * mm});
            skLineSegment(sketch, "E83.6.0.1", {"start": v(-21, 10) * mm, "end": v(-21, 50) * mm});
            skLineSegment(sketch, "E83.6.0.2", {"start": v(-21, 50) * mm, "end": v(-19, 50) * mm});
            skLineSegment(sketch, "E83.6.0.3", {"start": v(-21, 10) * mm, "end": v(-19, 10) * mm});
            skLineSegment(sketch, "E83.7.0.0", {"start": v(-15, 10) * mm, "end": v(-15, 50) * mm});
            skLineSegment(sketch, "E83.7.0.1", {"start": v(-17, 10) * mm, "end": v(-17, 50) * mm});
            skLineSegment(sketch, "E83.7.0.2", {"start": v(-17, 50) * mm, "end": v(-15, 50) * mm});
            skLineSegment(sketch, "E83.7.0.3", {"start": v(-17, 10) * mm, "end": v(-15, 10) * mm});
            skLineSegment(sketch, "E83.direction1", {"start": v(-45, 10) * mm, "end": v(-41, 10) * mm, "construction": true});
            skLineSegment(sketch, "E84.0.8.0", {"start": v(-11, 10) * mm, "end": v(-11, 50) * mm});
            skLineSegment(sketch, "E84.3.8.0", {"start": v(-13, 10) * mm, "end": v(-13, 50) * mm});
            skLineSegment(sketch, "E84.6.8.0", {"start": v(-13, 50) * mm, "end": v(-11, 50) * mm});
            skLineSegment(sketch, "E84.9.8.0", {"start": v(-13, 10) * mm, "end": v(-11, 10) * mm});
            skSolve(sketch);
        }
        {
            var Q0;
            Q0=qSketchRegion(id+"F12",true);
            extrude(context, id + "F13", {"entities" : qUnion([Q0]), "operationType" : NewBodyOperationType.REMOVE, "endBound" : BoundingType.UP_TO_NEXT, "oppositeDirection" : true, "depth" : 25 * mm});
        }
        {
            var Q0;
            Q0=makeQuery(id+"F3.opExtrude","CAP_EDGE",EDGE,{"disambiguationData":[OSD([sQuery(id+"F0.wireOp",EDGE,"E21.left")])],"isStart":false});
            var Q1;
            Q1=makeQuery(id+"F3.opExtrude","CAP_EDGE",EDGE,{"disambiguationData":[OSD([sQuery(id+"F0.wireOp",EDGE,"E22.bottom")])],"isStart":false});
            var Q2;
            Q2=makeQuery(id+"F3.opExtrude","CAP_EDGE",EDGE,{"disambiguationData":[OSD([sQuery(id+"F0.wireOp",EDGE,"E21.right")])],"isStart":false});
            var Q3;
            Q3=makeQuery(id+"F3.opExtrude","CAP_EDGE",EDGE,{"disambiguationData":[OSD([sQuery(id+"F0.wireOp",EDGE,"E22.top")])],"isStart":false});
            chamfer(context, id + "F14", {"entities" : qUnion([Q0, Q1, Q2, Q3]), "chamferType" : ChamferType.TWO_OFFSETS, "width1" : 3 * mm, "oppositeDirection" : false, "width2" : 20 * mm, "tangentPropagation" : true});
        }
        {
            var Q0;
            Q0=makeQuery(id+"F3.opExtrude","CAP_EDGE",EDGE,{"disambiguationData":[OSD([sQuery(id+"F0.wireOp",EDGE,"E16.top")])],"isStart":false});
            var Q1;
            Q1=makeQuery(id+"F3.opExtrude","CAP_EDGE",EDGE,{"disambiguationData":[OSD([sQuery(id+"F0.wireOp",EDGE,"E15.left")])],"isStart":false});
            var Q2;
            Q2=makeQuery(id+"F3.opExtrude","CAP_EDGE",EDGE,{"disambiguationData":[OSD([sQuery(id+"F0.wireOp",EDGE,"E15.right")])],"isStart":false});
            var Q3;
            Q3=makeQuery(id+"F3.opExtrude","CAP_EDGE",EDGE,{"disambiguationData":[OSD([sQuery(id+"F0.wireOp",EDGE,"E9.top")])],"isStart":false});
            var Q4;
            Q4=makeQuery(id+"F3.opExtrude","CAP_EDGE",EDGE,{"disambiguationData":[OSD([sQuery(id+"F0.wireOp",EDGE,"E10.right")])],"isStart":false});
            var Q5;
            Q5=makeQuery(id+"F3.opExtrude","CAP_EDGE",EDGE,{"disambiguationData":[OSD([sQuery(id+"F0.wireOp",EDGE,"E27.right")])],"isStart":false});
            var Q6;
            Q6=makeQuery(id+"F3.opExtrude","CAP_EDGE",EDGE,{"disambiguationData":[OSD([sQuery(id+"F0.wireOp",EDGE,"E28.bottom")])],"isStart":false});
            chamfer(context, id + "F15", {"entities" : qUnion([Q0, Q1, Q2, Q3, Q4, Q5, Q6]), "chamferType" : ChamferType.TWO_OFFSETS, "width1" : 20 * mm, "oppositeDirection" : false, "width2" : 3 * mm, "tangentPropagation" : true});
        }
        {
            var Q0;
            Q0=makeQuery(id+"F3.opExtrude","CAP_EDGE",EDGE,{"disambiguationData":[OSD([sQuery(id+"F0.wireOp",EDGE,"E27.left")])],"isStart":false});
            var Q1;
            Q1=makeQuery(id+"F3.opExtrude","CAP_EDGE",EDGE,{"disambiguationData":[OSD([sQuery(id+"F0.wireOp",EDGE,"E28.top")])],"isStart":false});
            var Q2;
            Q2=makeQuery(id+"F3.opExtrude","CAP_EDGE",EDGE,{"disambiguationData":[OSD([sQuery(id+"F0.wireOp",EDGE,"E10.left")])],"isStart":false});
            chamfer(context, id + "F16", {"entities" : qUnion([Q0, Q1, Q2]), "chamferType" : ChamferType.TWO_OFFSETS, "width1" : 3 * mm, "oppositeDirection" : false, "width2" : 20 * mm, "tangentPropagation" : true});
        }
        {
            var Q0;
            {var subQ3=sQuery(id+"F0.wireOp",EDGE,"E35");Q0=makeQuery(id+"F0.imprint","IMPRINT",FACE,{"disambiguationData":[TD([[makeQuery(id+"F0.imprint","IMPRINT",EDGE,{"derivedFrom":subQ3}),-1.0]])]});}
            var Q1;
            {var subQ3=sQuery(id+"F0.wireOp",EDGE,"E36");Q1=makeQuery(id+"F0.imprint","IMPRINT",FACE,{"disambiguationData":[TD([[makeQuery(id+"F0.imprint","IMPRINT",EDGE,{"derivedFrom":subQ3}),-1.0]])]});}
            var Q2;
            {var subQ3=sQuery(id+"F0.wireOp",EDGE,"E34");Q2=makeQuery(id+"F0.imprint","IMPRINT",FACE,{"disambiguationData":[TD([[makeQuery(id+"F0.imprint","IMPRINT",EDGE,{"derivedFrom":subQ3}),1.0]])]});}
            var Q3;
            {var subQ3=sQuery(id+"F0.wireOp",EDGE,"E33");Q3=makeQuery(id+"F0.imprint","IMPRINT",FACE,{"disambiguationData":[TD([[makeQuery(id+"F0.imprint","IMPRINT",EDGE,{"derivedFrom":subQ3}),-1.0]])]});}
            var Q4;
            Q4=makeQuery(id+"F1.opExtrude","CAP_FACE",FACE,{"disambiguationData":[OSD([sQuery(id+"F0.wireOp",EDGE,"E0.bottom"),sQuery(id+"F0.wireOp",EDGE,"E0.top"),sQuery(id+"F0.wireOp",EDGE,"E0.left"),sQuery(id+"F0.wireOp",EDGE,"E0.right")])],"isStart":false});
            extrude(context, id + "F17", {"entities" : qUnion([Q0, Q1, Q2, Q3]), "operationType" : NewBodyOperationType.ADD, "endBound" : BoundingType.UP_TO_SURFACE, "endBoundEntityFace" : qUnion([Q4]), "depth" : 25 * mm});
        }
        {
            var Q0;
            {var subQ0=sQuery(id+"F0.wireOp",EDGE,"E0.right");var subQ1=sQuery(id+"F0.wireOp",EDGE,"E0.top");var subQ2=sQuery(id+"F0.wireOp",EDGE,"E0.left");var subQ3=sQuery(id+"F0.wireOp",EDGE,"E0.bottom");Q0=makeQuery(id+"F17.boolean.opBoolean","MERGE",FACE,{"derivedFrom":[makeQuery(id+"F1.opExtrude","CAP_FACE",FACE,{"disambiguationData":[OSD([subQ3,subQ1,subQ2,subQ0])],"isStart":false}),makeQuery(id+"F17.opExtrude","CAP_FACE",FACE,{"disambiguationData":[OSD([subQ3,subQ1,subQ2,subQ0]),ownerDisambiguation([makeQuery(id+"F17.opExtrude","SWEPT_BODY",BODY,{"disambiguationData":[OSD([subQ3,subQ2,sQuery(id+"F0.wireOp",EDGE,"E34")])]})])],"isStart":false}),makeQuery(id+"F17.opExtrude","CAP_FACE",FACE,{"disambiguationData":[OSD([subQ3,subQ1,subQ2,subQ0]),ownerDisambiguation([makeQuery(id+"F17.opExtrude","SWEPT_BODY",BODY,{"disambiguationData":[OSD([subQ3,subQ0,sQuery(id+"F0.wireOp",EDGE,"E36")])]})])],"isStart":false}),makeQuery(id+"F17.opExtrude","CAP_FACE",FACE,{"disambiguationData":[OSD([subQ3,subQ1,subQ2,subQ0]),ownerDisambiguation([makeQuery(id+"F17.opExtrude","SWEPT_BODY",BODY,{"disambiguationData":[OSD([subQ1,subQ2,sQuery(id+"F0.wireOp",EDGE,"E33")])]})])],"isStart":false}),makeQuery(id+"F17.opExtrude","CAP_FACE",FACE,{"disambiguationData":[OSD([subQ3,subQ1,subQ2,subQ0]),ownerDisambiguation([makeQuery(id+"F17.opExtrude","SWEPT_BODY",BODY,{"disambiguationData":[OSD([subQ1,subQ0,sQuery(id+"F0.wireOp",EDGE,"E35")])]})])],"isStart":false})]});}
            var sketch = newSketch(context, id + "F18", { "sketchPlane" : qUnion([Q0])});
            skCircle(sketch, "E85", {"center": v(-61.9, -71.9) * mm, "radius": 1.45 * mm});
            skCircle(sketch, "E86", {"center": v(-61.9, 71.9) * mm, "radius": 1.45 * mm});
            skCircle(sketch, "E87", {"center": v(61.9, -71.9) * mm, "radius": 1.45 * mm});
            skCircle(sketch, "E88", {"center": v(61.9, 71.9) * mm, "radius": 1.45 * mm});
            skSolve(sketch);
        }
        {
            var Q0;
            Q0=qSketchRegion(id+"F18",true);
            extrude(context, id + "F19", {"entities" : qUnion([Q0]), "operationType" : NewBodyOperationType.REMOVE, "oppositeDirection" : true, "depth" : 15 * mm});
        }
        {
            var Q0;
            {var subQ0=sQuery(id+"F0.wireOp",EDGE,"E0.right");var subQ1=sQuery(id+"F0.wireOp",EDGE,"E0.top");var subQ2=sQuery(id+"F0.wireOp",EDGE,"E0.left");var subQ3=sQuery(id+"F0.wireOp",EDGE,"E0.bottom");Q0=makeQuery(id+"F17.boolean.opBoolean","MERGE",FACE,{"derivedFrom":[makeQuery(id+"F1.opExtrude","CAP_FACE",FACE,{"disambiguationData":[OSD([subQ3,subQ1,subQ2,subQ0])],"isStart":false}),makeQuery(id+"F17.opExtrude","CAP_FACE",FACE,{"disambiguationData":[OSD([subQ3,subQ1,subQ2,subQ0]),ownerDisambiguation([makeQuery(id+"F17.opExtrude","SWEPT_BODY",BODY,{"disambiguationData":[OSD([subQ3,subQ2,sQuery(id+"F0.wireOp",EDGE,"E34")])]})])],"isStart":false}),makeQuery(id+"F17.opExtrude","CAP_FACE",FACE,{"disambiguationData":[OSD([subQ3,subQ1,subQ2,subQ0]),ownerDisambiguation([makeQuery(id+"F17.opExtrude","SWEPT_BODY",BODY,{"disambiguationData":[OSD([subQ3,subQ0,sQuery(id+"F0.wireOp",EDGE,"E36")])]})])],"isStart":false}),makeQuery(id+"F17.opExtrude","CAP_FACE",FACE,{"disambiguationData":[OSD([subQ3,subQ1,subQ2,subQ0]),ownerDisambiguation([makeQuery(id+"F17.opExtrude","SWEPT_BODY",BODY,{"disambiguationData":[OSD([subQ1,subQ2,sQuery(id+"F0.wireOp",EDGE,"E33")])]})])],"isStart":false}),makeQuery(id+"F17.opExtrude","CAP_FACE",FACE,{"disambiguationData":[OSD([subQ3,subQ1,subQ2,subQ0]),ownerDisambiguation([makeQuery(id+"F17.opExtrude","SWEPT_BODY",BODY,{"disambiguationData":[OSD([subQ1,subQ0,sQuery(id+"F0.wireOp",EDGE,"E35")])]})])],"isStart":false})]});}
            var sketch = newSketch(context, id + "F20", { "sketchPlane" : qUnion([Q0])});
            skLineSegment(sketch, "E89.bottom", {"start": v(-65, 75) * mm, "end": v(65, 75) * mm});
            skLineSegment(sketch, "E89.top", {"start": v(-65, -75) * mm, "end": v(65, -75) * mm});
            skLineSegment(sketch, "E89.left", {"start": v(-65, 75) * mm, "end": v(-65, -75) * mm});
            skLineSegment(sketch, "E89.right", {"start": v(65, 75) * mm, "end": v(65, -75) * mm});
            skSolve(sketch);
        }
        {
            var Q0;
            Q0=qSketchRegion(id+"F20",true);
            extrude(context, id + "F21", {"entities" : qUnion([Q0]), "depth" : 2.5 * mm});
        }
        {
            var Q0;
            Q0=makeQuery(id+"F21.opExtrude","SWEPT_BODY",BODY,{"disambiguationData":[OSD([sQuery(id+"F20.wireOp",EDGE,"E89.bottom"),sQuery(id+"F20.wireOp",EDGE,"E89.top"),sQuery(id+"F20.wireOp",EDGE,"E89.left"),sQuery(id+"F20.wireOp",EDGE,"E89.right")])]});
            transform(context, id + "F22", {"entities" : qUnion([Q0]), "transformType" : TransformType.TRANSLATION_3D, "dx" : 0 * mm, "dy" : 0 * mm, "dz" : 75 * mm, "makeCopy" : false});
        }
        {
            var Q0;
            Q0=makeQuery(id+"F21.opExtrude","CAP_FACE",FACE,{"disambiguationData":[OSD([sQuery(id+"F20.wireOp",EDGE,"E89.bottom"),sQuery(id+"F20.wireOp",EDGE,"E89.top"),sQuery(id+"F20.wireOp",EDGE,"E89.left"),sQuery(id+"F20.wireOp",EDGE,"E89.right")])],"isStart":false});
            var sketch = newSketch(context, id + "F23", { "sketchPlane" : qUnion([Q0])});
            skCircle(sketch, "E90", {"center": v(61.9, -71.9) * mm, "radius": 1.6 * mm});
            skCircle(sketch, "E91", {"center": v(-61.9, -71.9) * mm, "radius": 1.6 * mm});
            skCircle(sketch, "E92", {"center": v(-61.9, 71.9) * mm, "radius": 1.6 * mm});
            skCircle(sketch, "E93", {"center": v(61.9, 71.9) * mm, "radius": 1.6 * mm});
            skCircle(sketch, "E94", {"center": v(-61.9, -71.9) * mm, "radius": 2.75 * mm});
            skCircle(sketch, "E95", {"center": v(61.9, -71.9) * mm, "radius": 2.75 * mm});
            skCircle(sketch, "E96", {"center": v(61.9, 71.9) * mm, "radius": 2.75 * mm});
            skCircle(sketch, "E97", {"center": v(-61.9, 71.9) * mm, "radius": 2.75 * mm});
            skSolve(sketch);
        }
        {
            var Q0;
            Q0=makeQuery(id+"F23.imprint","IMPRINT",FACE,{"disambiguationData":[TD([[makeQuery(id+"F23.imprint","IMPRINT",EDGE,{"derivedFrom":sQuery(id+"F23.wireOp",EDGE,"E91")}),1.0]])]});
            var Q1;
            Q1=makeQuery(id+"F23.imprint","IMPRINT",FACE,{"disambiguationData":[TD([[makeQuery(id+"F23.imprint","IMPRINT",EDGE,{"derivedFrom":sQuery(id+"F23.wireOp",EDGE,"E90")}),1.0]])]});
            var Q2;
            Q2=makeQuery(id+"F23.imprint","IMPRINT",FACE,{"disambiguationData":[TD([[makeQuery(id+"F23.imprint","IMPRINT",EDGE,{"derivedFrom":sQuery(id+"F23.wireOp",EDGE,"E93")}),1.0]])]});
            var Q3;
            Q3=makeQuery(id+"F23.imprint","IMPRINT",FACE,{"disambiguationData":[TD([[makeQuery(id+"F23.imprint","IMPRINT",EDGE,{"derivedFrom":sQuery(id+"F23.wireOp",EDGE,"E92")}),1.0]])]});
            extrude(context, id + "F24", {"entities" : qUnion([Q0, Q1, Q2, Q3]), "operationType" : NewBodyOperationType.REMOVE, "endBound" : BoundingType.UP_TO_NEXT, "oppositeDirection" : true, "depth" : 25 * mm});
        }
        {
            var Q0;
            Q0=makeQuery(id+"F1.opExtrude","SWEPT_EDGE",EDGE,{"disambiguationData":[OSD([sQuery(id+"F0.wireOp",EDGE,"E0.bottom"),sQuery(id+"F0.wireOp",EDGE,"E0.left")])]});
            var Q1;
            Q1=makeQuery(id+"F1.opExtrude","SWEPT_EDGE",EDGE,{"disambiguationData":[OSD([sQuery(id+"F0.wireOp",EDGE,"E0.bottom"),sQuery(id+"F0.wireOp",EDGE,"E0.right")])]});
            var Q2;
            Q2=makeQuery(id+"F1.opExtrude","SWEPT_EDGE",EDGE,{"disambiguationData":[OSD([sQuery(id+"F0.wireOp",EDGE,"E0.top"),sQuery(id+"F0.wireOp",EDGE,"E0.left")])]});
            var Q3;
            Q3=makeQuery(id+"F1.opExtrude","SWEPT_EDGE",EDGE,{"disambiguationData":[OSD([sQuery(id+"F0.wireOp",EDGE,"E0.top"),sQuery(id+"F0.wireOp",EDGE,"E0.right")])]});
            var Q4;
            Q4=makeQuery(id+"F1.opExtrude","CAP_EDGE",EDGE,{"disambiguationData":[OSD([sQuery(id+"F0.wireOp",EDGE,"E0.right")])],"isStart":true});
            var Q5;
            Q5=makeQuery(id+"F21.opExtrude","SWEPT_EDGE",EDGE,{"disambiguationData":[OSD([sQuery(id+"F20.wireOp",EDGE,"E89.top"),sQuery(id+"F20.wireOp",EDGE,"E89.right")])]});
            var Q6;
            Q6=makeQuery(id+"F21.opExtrude","SWEPT_EDGE",EDGE,{"disambiguationData":[OSD([sQuery(id+"F20.wireOp",EDGE,"E89.bottom"),sQuery(id+"F20.wireOp",EDGE,"E89.right")])]});
            var Q7;
            Q7=makeQuery(id+"F21.opExtrude","SWEPT_EDGE",EDGE,{"disambiguationData":[OSD([sQuery(id+"F20.wireOp",EDGE,"E89.bottom"),sQuery(id+"F20.wireOp",EDGE,"E89.left")])]});
            var Q8;
            Q8=makeQuery(id+"F21.opExtrude","SWEPT_EDGE",EDGE,{"disambiguationData":[OSD([sQuery(id+"F20.wireOp",EDGE,"E89.top"),sQuery(id+"F20.wireOp",EDGE,"E89.left")])]});
            fillet(context, id + "F25", {"entities" : qUnion([Q0, Q1, Q2, Q3, Q4, Q5, Q6, Q7, Q8]), "radius" : 1 * mm, "tangentPropagation" : true, "allowEdgeOverflow" : false});
        }
        {
            var Q0;
            Q0=makeQuery(id+"F13.boolean.opBoolean","COPY",EDGE,{"derivedFrom":makeQuery(id+"F13.opExtrude","SWEPT_EDGE",EDGE,{"disambiguationData":[OSD([sQuery(id+"F12.wireOp",EDGE,"E82.bottom"),sQuery(id+"F12.wireOp",EDGE,"E82.right")])]})});
            var Q1;
            Q1=makeQuery(id+"F13.boolean.opBoolean","COPY",EDGE,{"derivedFrom":makeQuery(id+"F13.opExtrude","SWEPT_EDGE",EDGE,{"disambiguationData":[OSD([sQuery(id+"F12.wireOp",EDGE,"E82.bottom"),sQuery(id+"F12.wireOp",EDGE,"E82.left")])]})});
            var Q2;
            Q2=makeQuery(id+"F13.boolean.opBoolean","COPY",EDGE,{"derivedFrom":makeQuery(id+"F13.opExtrude","SWEPT_EDGE",EDGE,{"disambiguationData":[OSD([sQuery(id+"F12.wireOp",EDGE,"E83.1.0.1"),sQuery(id+"F12.wireOp",EDGE,"E83.1.0.3")])]})});
            var Q3;
            Q3=makeQuery(id+"F13.boolean.opBoolean","COPY",EDGE,{"derivedFrom":makeQuery(id+"F13.opExtrude","SWEPT_EDGE",EDGE,{"disambiguationData":[OSD([sQuery(id+"F12.wireOp",EDGE,"E83.1.0.0"),sQuery(id+"F12.wireOp",EDGE,"E83.1.0.3")])]})});
            var Q4;
            Q4=makeQuery(id+"F13.boolean.opBoolean","COPY",EDGE,{"derivedFrom":makeQuery(id+"F13.opExtrude","SWEPT_EDGE",EDGE,{"disambiguationData":[OSD([sQuery(id+"F12.wireOp",EDGE,"E83.6.0.0"),sQuery(id+"F12.wireOp",EDGE,"E83.6.0.3")])]})});
            var Q5;
            Q5=makeQuery(id+"F13.boolean.opBoolean","COPY",EDGE,{"derivedFrom":makeQuery(id+"F13.opExtrude","SWEPT_EDGE",EDGE,{"disambiguationData":[OSD([sQuery(id+"F12.wireOp",EDGE,"E83.2.0.0"),sQuery(id+"F12.wireOp",EDGE,"E83.2.0.3")])]})});
            var Q6;
            Q6=makeQuery(id+"F13.boolean.opBoolean","COPY",EDGE,{"derivedFrom":makeQuery(id+"F13.opExtrude","SWEPT_EDGE",EDGE,{"disambiguationData":[OSD([sQuery(id+"F12.wireOp",EDGE,"E83.6.0.1"),sQuery(id+"F12.wireOp",EDGE,"E83.6.0.3")])]})});
            var Q7;
            Q7=makeQuery(id+"F13.boolean.opBoolean","COPY",EDGE,{"derivedFrom":makeQuery(id+"F13.opExtrude","SWEPT_EDGE",EDGE,{"disambiguationData":[OSD([sQuery(id+"F12.wireOp",EDGE,"E83.4.0.1"),sQuery(id+"F12.wireOp",EDGE,"E83.4.0.3")])]})});
            var Q8;
            Q8=makeQuery(id+"F13.boolean.opBoolean","COPY",EDGE,{"derivedFrom":makeQuery(id+"F13.opExtrude","SWEPT_EDGE",EDGE,{"disambiguationData":[OSD([sQuery(id+"F12.wireOp",EDGE,"E83.3.0.1"),sQuery(id+"F12.wireOp",EDGE,"E83.3.0.3")])]})});
            var Q9;
            Q9=makeQuery(id+"F13.boolean.opBoolean","COPY",EDGE,{"derivedFrom":makeQuery(id+"F13.opExtrude","SWEPT_EDGE",EDGE,{"disambiguationData":[OSD([sQuery(id+"F12.wireOp",EDGE,"E83.5.0.1"),sQuery(id+"F12.wireOp",EDGE,"E83.5.0.3")])]})});
            var Q10;
            Q10=makeQuery(id+"F13.boolean.opBoolean","COPY",EDGE,{"derivedFrom":makeQuery(id+"F13.opExtrude","SWEPT_EDGE",EDGE,{"disambiguationData":[OSD([sQuery(id+"F12.wireOp",EDGE,"E83.7.0.1"),sQuery(id+"F12.wireOp",EDGE,"E83.7.0.3")])]})});
            var Q11;
            Q11=makeQuery(id+"F13.boolean.opBoolean","COPY",EDGE,{"derivedFrom":makeQuery(id+"F13.opExtrude","SWEPT_EDGE",EDGE,{"disambiguationData":[OSD([sQuery(id+"F12.wireOp",EDGE,"E83.3.0.0"),sQuery(id+"F12.wireOp",EDGE,"E83.3.0.3")])]})});
            var Q12;
            Q12=makeQuery(id+"F13.boolean.opBoolean","COPY",EDGE,{"derivedFrom":makeQuery(id+"F13.opExtrude","SWEPT_EDGE",EDGE,{"disambiguationData":[OSD([sQuery(id+"F12.wireOp",EDGE,"E83.5.0.0"),sQuery(id+"F12.wireOp",EDGE,"E83.5.0.3")])]})});
            var Q13;
            Q13=makeQuery(id+"F13.boolean.opBoolean","COPY",EDGE,{"derivedFrom":makeQuery(id+"F13.opExtrude","SWEPT_EDGE",EDGE,{"disambiguationData":[OSD([sQuery(id+"F12.wireOp",EDGE,"E83.2.0.1"),sQuery(id+"F12.wireOp",EDGE,"E83.2.0.3")])]})});
            var Q14;
            Q14=makeQuery(id+"F13.boolean.opBoolean","COPY",EDGE,{"derivedFrom":makeQuery(id+"F13.opExtrude","SWEPT_EDGE",EDGE,{"disambiguationData":[OSD([sQuery(id+"F12.wireOp",EDGE,"E83.4.0.0"),sQuery(id+"F12.wireOp",EDGE,"E83.4.0.3")])]})});
            var Q15;
            Q15=makeQuery(id+"F13.boolean.opBoolean","COPY",EDGE,{"derivedFrom":makeQuery(id+"F13.opExtrude","SWEPT_EDGE",EDGE,{"disambiguationData":[OSD([sQuery(id+"F12.wireOp",EDGE,"E83.7.0.0"),sQuery(id+"F12.wireOp",EDGE,"E83.7.0.3")])]})});
            var Q16;
            Q16=makeQuery(id+"F13.boolean.opBoolean","COPY",EDGE,{"derivedFrom":makeQuery(id+"F13.opExtrude","SWEPT_EDGE",EDGE,{"disambiguationData":[OSD([sQuery(id+"F12.wireOp",EDGE,"E83.7.0.0"),sQuery(id+"F12.wireOp",EDGE,"E83.7.0.2")])]})});
            var Q17;
            Q17=makeQuery(id+"F13.boolean.opBoolean","COPY",EDGE,{"derivedFrom":makeQuery(id+"F13.opExtrude","SWEPT_EDGE",EDGE,{"disambiguationData":[OSD([sQuery(id+"F12.wireOp",EDGE,"E83.6.0.0"),sQuery(id+"F12.wireOp",EDGE,"E83.6.0.2")])]})});
            var Q18;
            Q18=makeQuery(id+"F13.boolean.opBoolean","COPY",EDGE,{"derivedFrom":makeQuery(id+"F13.opExtrude","SWEPT_EDGE",EDGE,{"disambiguationData":[OSD([sQuery(id+"F12.wireOp",EDGE,"E83.5.0.0"),sQuery(id+"F12.wireOp",EDGE,"E83.5.0.2")])]})});
            var Q19;
            Q19=makeQuery(id+"F13.boolean.opBoolean","COPY",EDGE,{"derivedFrom":makeQuery(id+"F13.opExtrude","SWEPT_EDGE",EDGE,{"disambiguationData":[OSD([sQuery(id+"F12.wireOp",EDGE,"E83.4.0.0"),sQuery(id+"F12.wireOp",EDGE,"E83.4.0.2")])]})});
            var Q20;
            Q20=makeQuery(id+"F13.boolean.opBoolean","COPY",EDGE,{"derivedFrom":makeQuery(id+"F13.opExtrude","SWEPT_EDGE",EDGE,{"disambiguationData":[OSD([sQuery(id+"F12.wireOp",EDGE,"E83.3.0.0"),sQuery(id+"F12.wireOp",EDGE,"E83.3.0.2")])]})});
            var Q21;
            Q21=makeQuery(id+"F13.boolean.opBoolean","COPY",EDGE,{"derivedFrom":makeQuery(id+"F13.opExtrude","SWEPT_EDGE",EDGE,{"disambiguationData":[OSD([sQuery(id+"F12.wireOp",EDGE,"E83.2.0.0"),sQuery(id+"F12.wireOp",EDGE,"E83.2.0.2")])]})});
            var Q22;
            Q22=makeQuery(id+"F13.boolean.opBoolean","COPY",EDGE,{"derivedFrom":makeQuery(id+"F13.opExtrude","SWEPT_EDGE",EDGE,{"disambiguationData":[OSD([sQuery(id+"F12.wireOp",EDGE,"E83.1.0.0"),sQuery(id+"F12.wireOp",EDGE,"E83.1.0.2")])]})});
            var Q23;
            Q23=makeQuery(id+"F13.boolean.opBoolean","COPY",EDGE,{"derivedFrom":makeQuery(id+"F13.opExtrude","SWEPT_EDGE",EDGE,{"disambiguationData":[OSD([sQuery(id+"F12.wireOp",EDGE,"E82.top"),sQuery(id+"F12.wireOp",EDGE,"E82.right")])]})});
            var Q24;
            Q24=makeQuery(id+"F13.boolean.opBoolean","COPY",EDGE,{"derivedFrom":makeQuery(id+"F13.opExtrude","SWEPT_EDGE",EDGE,{"disambiguationData":[OSD([sQuery(id+"F12.wireOp",EDGE,"E82.top"),sQuery(id+"F12.wireOp",EDGE,"E82.left")])]})});
            var Q25;
            Q25=makeQuery(id+"F13.boolean.opBoolean","COPY",EDGE,{"derivedFrom":makeQuery(id+"F13.opExtrude","SWEPT_EDGE",EDGE,{"disambiguationData":[OSD([sQuery(id+"F12.wireOp",EDGE,"E83.1.0.1"),sQuery(id+"F12.wireOp",EDGE,"E83.1.0.2")])]})});
            var Q26;
            Q26=makeQuery(id+"F13.boolean.opBoolean","COPY",EDGE,{"derivedFrom":makeQuery(id+"F13.opExtrude","SWEPT_EDGE",EDGE,{"disambiguationData":[OSD([sQuery(id+"F12.wireOp",EDGE,"E83.2.0.1"),sQuery(id+"F12.wireOp",EDGE,"E83.2.0.2")])]})});
            var Q27;
            Q27=makeQuery(id+"F13.boolean.opBoolean","COPY",EDGE,{"derivedFrom":makeQuery(id+"F13.opExtrude","SWEPT_EDGE",EDGE,{"disambiguationData":[OSD([sQuery(id+"F12.wireOp",EDGE,"E83.3.0.1"),sQuery(id+"F12.wireOp",EDGE,"E83.3.0.2")])]})});
            var Q28;
            Q28=makeQuery(id+"F13.boolean.opBoolean","COPY",EDGE,{"derivedFrom":makeQuery(id+"F13.opExtrude","SWEPT_EDGE",EDGE,{"disambiguationData":[OSD([sQuery(id+"F12.wireOp",EDGE,"E83.4.0.1"),sQuery(id+"F12.wireOp",EDGE,"E83.4.0.2")])]})});
            var Q29;
            Q29=makeQuery(id+"F13.boolean.opBoolean","COPY",EDGE,{"derivedFrom":makeQuery(id+"F13.opExtrude","SWEPT_EDGE",EDGE,{"disambiguationData":[OSD([sQuery(id+"F12.wireOp",EDGE,"E83.5.0.1"),sQuery(id+"F12.wireOp",EDGE,"E83.5.0.2")])]})});
            var Q30;
            Q30=makeQuery(id+"F13.boolean.opBoolean","COPY",EDGE,{"derivedFrom":makeQuery(id+"F13.opExtrude","SWEPT_EDGE",EDGE,{"disambiguationData":[OSD([sQuery(id+"F12.wireOp",EDGE,"E83.6.0.1"),sQuery(id+"F12.wireOp",EDGE,"E83.6.0.2")])]})});
            var Q31;
            Q31=makeQuery(id+"F13.boolean.opBoolean","COPY",EDGE,{"derivedFrom":makeQuery(id+"F13.opExtrude","SWEPT_EDGE",EDGE,{"disambiguationData":[OSD([sQuery(id+"F12.wireOp",EDGE,"E83.7.0.1"),sQuery(id+"F12.wireOp",EDGE,"E83.7.0.2")])]})});
            var Q32;
            Q32=makeQuery(id+"F13.boolean.opBoolean","COPY",EDGE,{"derivedFrom":makeQuery(id+"F13.opExtrude","SWEPT_EDGE",EDGE,{"disambiguationData":[OSD([sQuery(id+"F12.wireOp",EDGE,"E84.3.8.0"),sQuery(id+"F12.wireOp",EDGE,"E84.9.8.0")])]})});
            var Q33;
            Q33=makeQuery(id+"F13.boolean.opBoolean","COPY",EDGE,{"derivedFrom":makeQuery(id+"F13.opExtrude","SWEPT_EDGE",EDGE,{"disambiguationData":[OSD([sQuery(id+"F12.wireOp",EDGE,"E84.0.8.0"),sQuery(id+"F12.wireOp",EDGE,"E84.9.8.0")])]})});
            var Q34;
            Q34=makeQuery(id+"F13.boolean.opBoolean","COPY",EDGE,{"derivedFrom":makeQuery(id+"F13.opExtrude","SWEPT_EDGE",EDGE,{"disambiguationData":[OSD([sQuery(id+"F12.wireOp",EDGE,"E84.0.8.0"),sQuery(id+"F12.wireOp",EDGE,"E84.6.8.0")])]})});
            var Q35;
            Q35=makeQuery(id+"F13.boolean.opBoolean","COPY",EDGE,{"derivedFrom":makeQuery(id+"F13.opExtrude","SWEPT_EDGE",EDGE,{"disambiguationData":[OSD([sQuery(id+"F12.wireOp",EDGE,"E84.3.8.0"),sQuery(id+"F12.wireOp",EDGE,"E84.6.8.0")])]})});
            fillet(context, id + "F26", {"entities" : qUnion([Q0, Q1, Q2, Q3, Q4, Q5, Q6, Q7, Q8, Q9, Q10, Q11, Q12, Q13, Q14, Q15, Q16, Q17, Q18, Q19, Q20, Q21, Q22, Q23, Q24, Q25, Q26, Q27, Q28, Q29, Q30, Q31, Q32, Q33, Q34, Q35]), "radius" : 1 * mm, "tangentPropagation" : true, "allowEdgeOverflow" : false});
        }
    });
